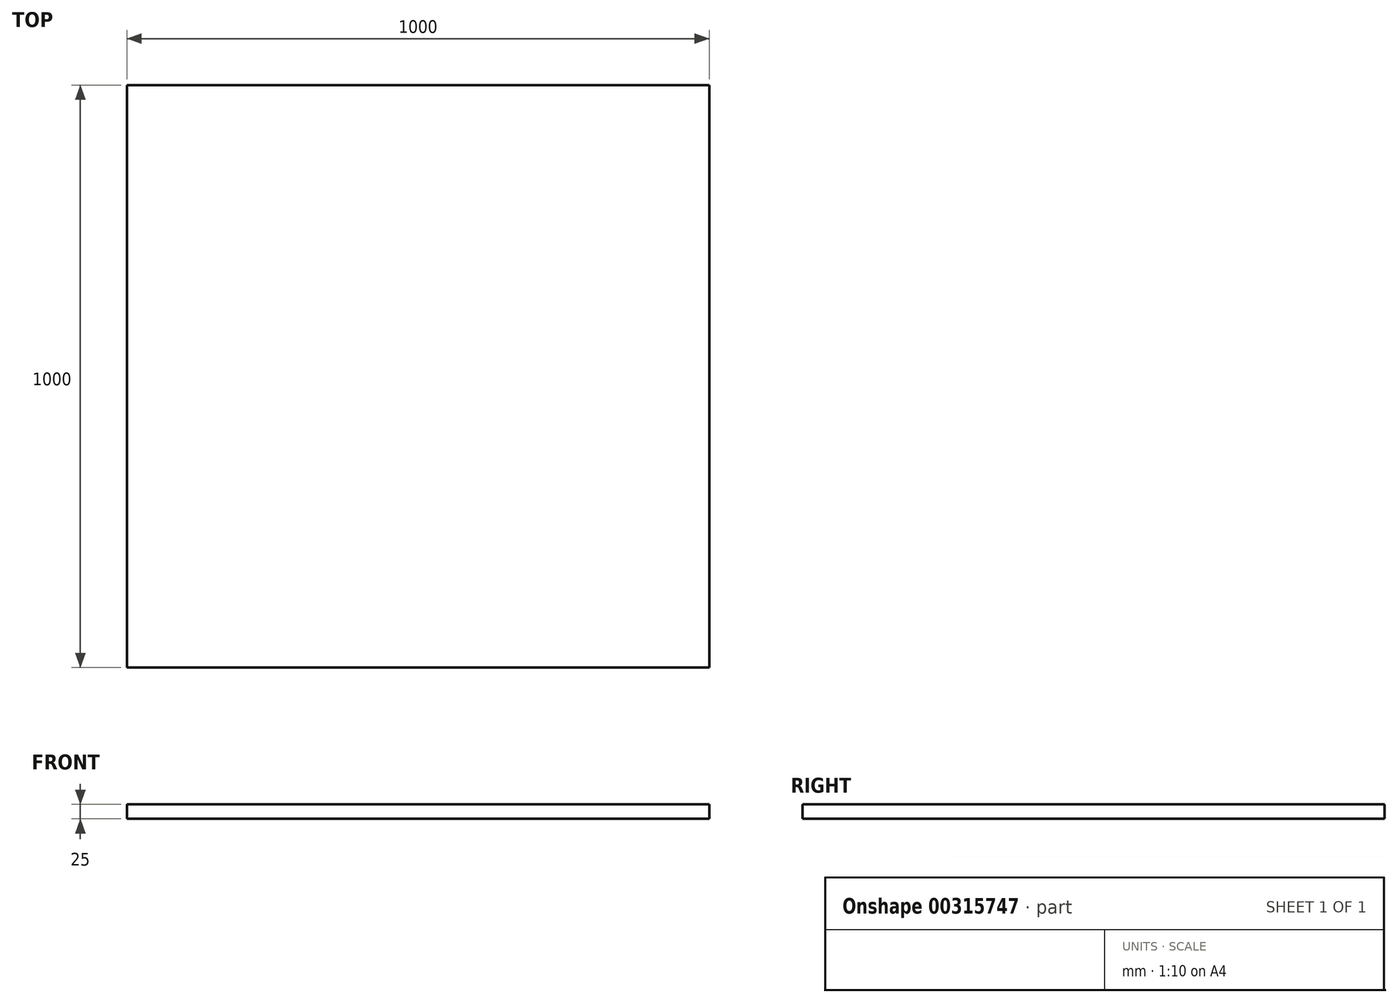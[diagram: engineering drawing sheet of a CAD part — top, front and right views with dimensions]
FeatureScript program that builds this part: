
annotation { "Feature Type Name" : "Feature", "Feature Type Description" : "" }
export const myFeature = defineFeature(function(context is Context, id is Id, definition is map)
    precondition{}
    {
        {
            var Q0;
            Q0=qCreatedBy(makeId("Top.planeOp"),FACE);
            var sketch = newSketch(context, id + "F0", { "sketchPlane" : qUnion([Q0])});
            skLineSegment(sketch, "E0.bottom", {"start": v(-500, 500) * mm, "end": v(500, 500) * mm});
            skLineSegment(sketch, "E0.top", {"start": v(-500, -500) * mm, "end": v(500, -500) * mm});
            skLineSegment(sketch, "E0.left", {"start": v(-500, 500) * mm, "end": v(-500, -500) * mm});
            skLineSegment(sketch, "E0.right", {"start": v(500, 500) * mm, "end": v(500, -500) * mm});
            skLineSegment(sketch, "E1", {"start": v(0, 0) * mm, "end": v(293.84, 0) * mm, "construction": true});
            skLineSegment(sketch, "E2", {"start": v(0, 0) * mm, "end": v(0, 344) * mm, "construction": true});
            skSolve(sketch);
        }
        {
            var Q0;
            Q0=makeQuery(id+"F0.imprint","IMPRINT",FACE,{"disambiguationData":[TD([[makeQuery(id+"F0.imprint","IMPRINT",EDGE,{"derivedFrom":sQuery(id+"F0.wireOp",EDGE,"E0.bottom")}),-1.0]])]});
            extrude(context, id + "F1", {"entities" : qUnion([Q0]), "depth" : 25 * mm});
        }
    });
